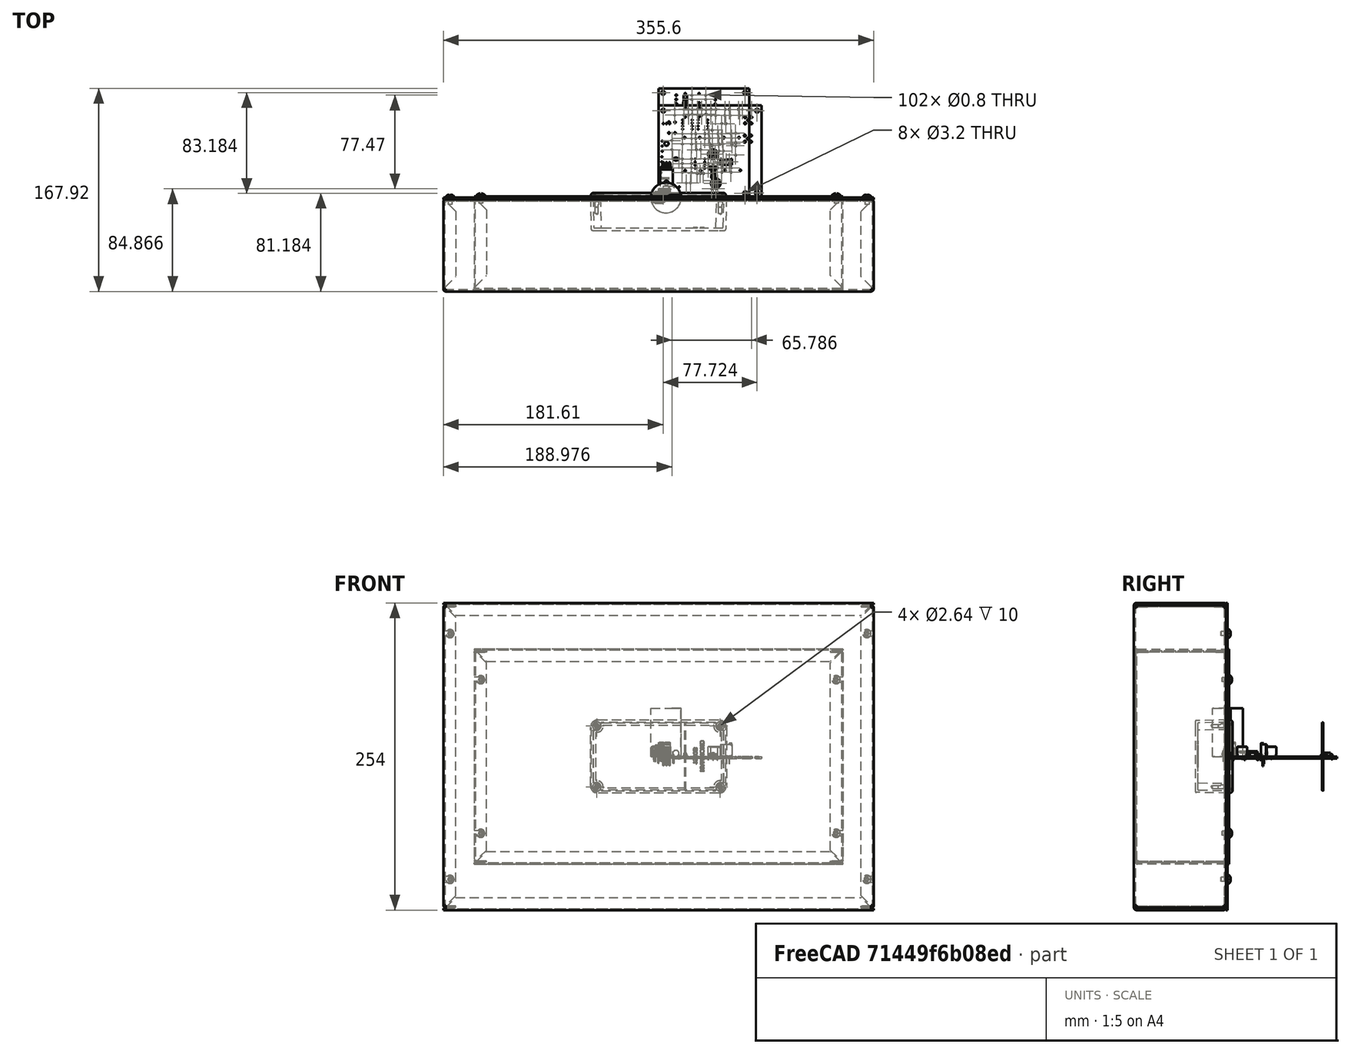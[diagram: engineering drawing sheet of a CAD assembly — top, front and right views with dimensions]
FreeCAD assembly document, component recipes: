
FREECAD ASSEMBLY — COMPONENT RECIPES ("hammond-enclosure")

This assembly document has 7 components, labeled P0..P6 below (a component is one placed body or linked part). 0 of them carry a construction recipe — the FreeCAD feature program that regenerates the part from scratch, quoted from this document or its linked companion documents; the rest are supplied as boundary geometry only. No exploded tour is included for this assembly.
COMPONENT P0 — geometry summary ("timebase"; no construction recipe available for this part):
  bounding box: 85.3 x 76.5 x 17.5 mm
  tessellated surface: 130,142 triangles
  volume: 16471 mm^3 (14% of its bounding box)
COMPONENT P1 — geometry summary ("15v-supply"; no construction recipe available for this part):
  bounding box: 90.4 x 75.2 x 47.9 mm
  tessellated surface: 64,468 triangles
  volume: 94218 mm^3 (29% of its bounding box)
COMPONENT P2 — geometry summary ("1444-1274"; no construction recipe available for this part):
  bounding box: 304.8 x 177.8 x 79.7 mm
  tessellated surface: 15,780 triangles
  volume: 193653 mm^3 (4% of its bounding box)
  symmetry: 2-fold rotationally symmetric about the x axis; 2-fold rotationally symmetric about the y axis; 2-fold rotationally symmetric about the z axis; mirror-symmetric across its x mid-plane, y mid-plane, z mid-plane
COMPONENT P3 — geometry summary ("1444-14104"; no construction recipe available for this part):
  bounding box: 355.6 x 254.0 x 80.0 mm
  tessellated surface: 16,236 triangles
  volume: 366253 mm^3 (5% of its bounding box)
  symmetry: 2-fold rotationally symmetric about the x axis; 2-fold rotationally symmetric about the y axis; 2-fold rotationally symmetric about the z axis; mirror-symmetric across its x mid-plane, y mid-plane, z mid-plane
COMPONENT P4 — geometry summary ("1590B-1"; no construction recipe available for this part):
  bounding box: 112.4 x 60.5 x 31.0 mm
  tessellated surface: 36,208 triangles
  volume: 50075 mm^3 (24% of its bounding box)
  symmetry: 2-fold rotationally symmetric about the y axis; mirror-symmetric across its x mid-plane, z mid-plane
COMPONENT P5 — geometry summary ("1590B-2"; no construction recipe available for this part):
  bounding box: 112.4 x 60.5 x 31.0 mm
  tessellated surface: 36,208 triangles
  volume: 50075 mm^3 (24% of its bounding box)
  symmetry: 2-fold rotationally symmetric about the y axis; mirror-symmetric across its x mid-plane, z mid-plane
COMPONENT P6 — geometry summary ("1590B-3"; no construction recipe available for this part):
  bounding box: 112.4 x 60.5 x 31.0 mm
  tessellated surface: 36,208 triangles
  volume: 50075 mm^3 (24% of its bounding box)
  symmetry: 2-fold rotationally symmetric about the y axis; mirror-symmetric across its x mid-plane, z mid-plane
PROVENANCE & LICENSES
A FreeCAD (.FCStd) document from a public repository crawl; recipes are the document's own serialized feature recipes (and, for linked parts, companion documents' recipes).
License: as declared in the source repository (recorded in the dataset sidecar).
